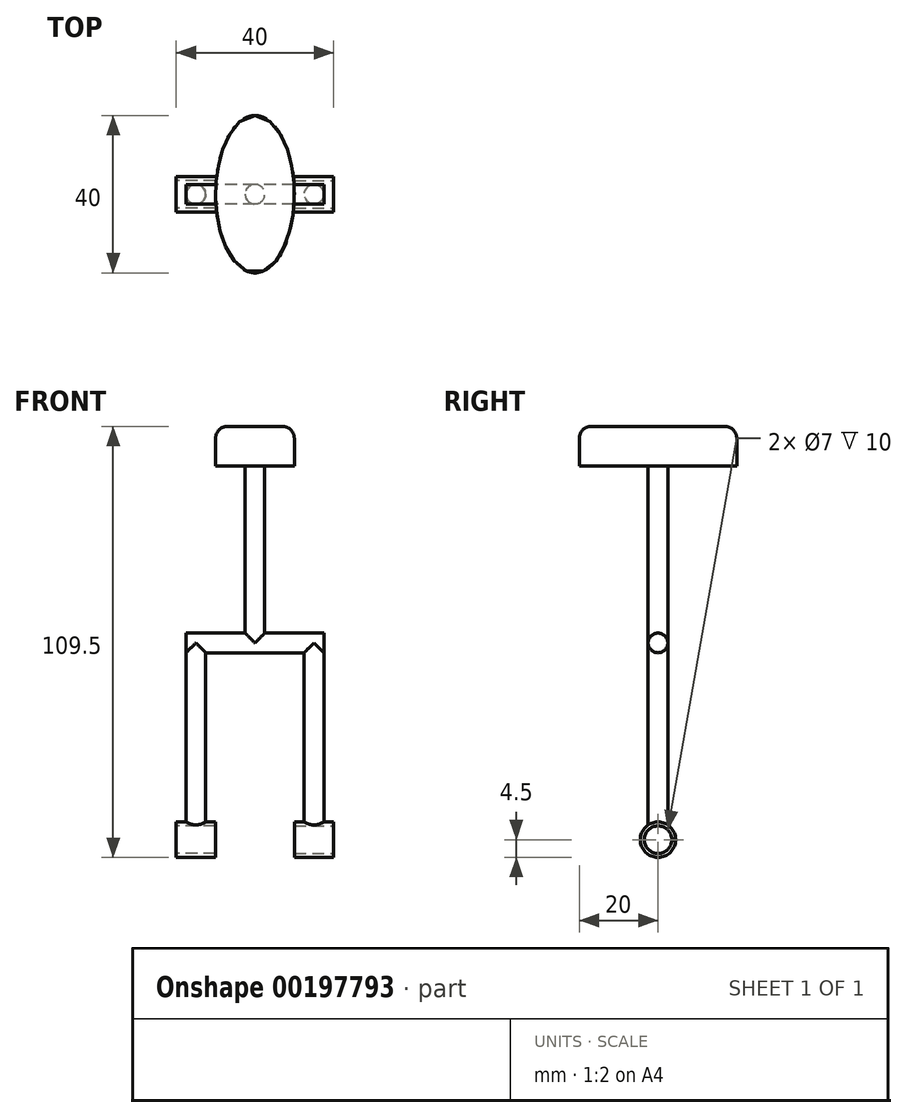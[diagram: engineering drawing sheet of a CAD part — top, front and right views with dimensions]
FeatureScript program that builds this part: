
annotation { "Feature Type Name" : "Feature", "Feature Type Description" : "" }
export const myFeature = defineFeature(function(context is Context, id is Id, definition is map)
    precondition{}
    {
        {
            var Q0;
            Q0=qCreatedBy(makeId("Top.planeOp"),FACE);
            var sketch = newSketch(context, id + "F0", { "sketchPlane" : qUnion([Q0])});
            skEllipse(sketch, "E0", {"center": v(0, 0) * mm, "majorRadius": 20 * mm, "minorRadius": 10 * mm, "majorAxis": v(0, 1)});
            skLineSegment(sketch, "E1", {"start": v(0, 0) * mm, "end": v(0, 20) * mm, "construction": true});
            skSolve(sketch);
        }
        {
            var Q0;
            Q0 = qSketchRegion(id + "F0", true);
            extrude(context, id + "F1", {"entities" : qUnion([Q0]), "depth" : 10 * mm});
        }
        {
            var Q0;
            Q0=makeQuery(id+"F1.opExtrude","CAP_FACE",FACE,{"disambiguationData":[OSD([sQuery(id+"F0.wireOp",EDGE,"E0")])],"isStart":true});
            var sketch = newSketch(context, id + "F2", { "sketchPlane" : qUnion([Q0])});
            skCircle(sketch, "E2", {"center": v(0, 0) * mm, "radius": 2.5 * mm});
            skSolve(sketch);
        }
        {
            var Q0;
            Q0 = qSketchRegion(id + "F2", true);
            extrude(context, id + "F3", {"entities" : qUnion([Q0]), "operationType" : NewBodyOperationType.ADD, "depth" : 45 * mm});
        }
        {
            var Q0;
            Q0=qCreatedBy(makeId("Right.planeOp"),FACE);
            var sketch = newSketch(context, id + "F4", { "sketchPlane" : qUnion([Q0])});
            skCircle(sketch, "E3", {"center": v(0, -45) * mm, "radius": 2.5 * mm});
            skSolve(sketch);
        }
        {
            var Q0;
            Q0 = qSketchRegion(id + "F4", true);
            extrude(context, id + "F5", {"entities" : qUnion([Q0]), "operationType" : NewBodyOperationType.ADD, "depth" : 17.5 * mm, "hasSecondDirection" : true, "secondDirectionOppositeDirection" : true, "secondDirectionDepth" : 17.5 * mm});
        }
        {
            var Q0;
            Q0=qCreatedBy(makeId("Top.planeOp"),FACE);
            cPlane(context, id + "F6", {"entities" : qUnion([Q0]), "cplaneType" : CPlaneType.OFFSET, "offset" : 45 * mm, "oppositeDirection" : true, "width" : 150 * mm, "height" : 150 * mm});
        }
        {
            var Q0;
            Q0=qCreatedBy(id+"F6.planeOp",FACE);
            var sketch = newSketch(context, id + "F7", { "sketchPlane" : qUnion([Q0])});
            skCircle(sketch, "E4", {"center": v(15, 0) * mm, "radius": 2.5 * mm});
            skCircle(sketch, "E5", {"center": v(-15, 0) * mm, "radius": 2.5 * mm});
            skSolve(sketch);
        }
        {
            var Q0;
            Q0 = qSketchRegion(id + "F7", true);
            extrude(context, id + "F8", {"entities" : qUnion([Q0]), "operationType" : NewBodyOperationType.ADD, "oppositeDirection" : true, "depth" : 50 * mm});
        }
        {
            var Q0;
            Q0=makeQuery(id+"F1.opExtrude","SWEPT_BODY",BODY,{"disambiguationData":[OSD([sQuery(id+"F0.wireOp",EDGE,"E0")])]});
            transform(context, id + "F9", {"entities" : qUnion([Q0]), "transformType" : TransformType.TRANSLATION_3D, "dx" : 0 * mm, "dy" : 0 * mm, "dz" : 45 * mm, "makeCopy" : false});
        }
        {
            var Q0;
            Q0=qCreatedBy(makeId("Right.planeOp"),FACE);
            cPlane(context, id + "F10", {"entities" : qUnion([Q0]), "cplaneType" : CPlaneType.OFFSET, "offset" : 15 * mm, "width" : 150 * mm, "height" : 150 * mm});
        }
        {
            var Q0;
            Q0=qCreatedBy(makeId("Right.planeOp"),FACE);
            cPlane(context, id + "F11", {"entities" : qUnion([Q0]), "cplaneType" : CPlaneType.OFFSET, "offset" : 15 * mm, "oppositeDirection" : true, "width" : 150 * mm, "height" : 150 * mm});
        }
        {
            var Q0;
            Q0=qCreatedBy(id+"F10.planeOp",FACE);
            var sketch = newSketch(context, id + "F12", { "sketchPlane" : qUnion([Q0])});
            skCircle(sketch, "E6", {"center": v(0, -50) * mm, "radius": 4.5 * mm});
            skSolve(sketch);
        }
        {
            var Q0;
            Q0 = qSketchRegion(id + "F12", true);
            extrude(context, id + "F13", {"entities" : qUnion([Q0]), "operationType" : NewBodyOperationType.ADD, "depth" : 5 * mm, "hasSecondDirection" : true, "secondDirectionOppositeDirection" : true, "secondDirectionDepth" : 5 * mm});
        }
        {
            var Q0;
            Q0=makeQuery(id+"F13.opExtrude","CAP_FACE",FACE,{"disambiguationData":[OSD([sQuery(id+"F12.wireOp",EDGE,"E6")])],"isStart":false});
            var sketch = newSketch(context, id + "F14", { "sketchPlane" : qUnion([Q0])});
            skCircle(sketch, "E7", {"center": v(0, -50) * mm, "radius": 3.5 * mm});
            skSolve(sketch);
        }
        {
            var Q0;
            Q0 = qSketchRegion(id + "F14", true);
            extrude(context, id + "F15", {"entities" : qUnion([Q0]), "operationType" : NewBodyOperationType.REMOVE, "oppositeDirection" : true, "depth" : 25 * mm});
        }
        {
            var Q0;
            Q0=qCreatedBy(id+"F11.planeOp",FACE);
            var sketch = newSketch(context, id + "F16", { "sketchPlane" : qUnion([Q0])});
            skCircle(sketch, "E8", {"center": v(0, -50) * mm, "radius": 4.5 * mm});
            skSolve(sketch);
        }
        {
            var Q0;
            Q0 = qSketchRegion(id + "F16", true);
            extrude(context, id + "F17", {"entities" : qUnion([Q0]), "operationType" : NewBodyOperationType.ADD, "depth" : 5 * mm, "hasSecondDirection" : true, "secondDirectionOppositeDirection" : true, "secondDirectionDepth" : 5 * mm});
        }
        {
            var Q0;
            Q0=makeQuery(id+"F17.opExtrude","CAP_FACE",FACE,{"disambiguationData":[OSD([sQuery(id+"F16.wireOp",EDGE,"E8")])],"isStart":true});
            var sketch = newSketch(context, id + "F18", { "sketchPlane" : qUnion([Q0])});
            skCircle(sketch, "E9", {"center": v(0, -50) * mm, "radius": 3.5 * mm});
            skSolve(sketch);
        }
        {
            var Q0;
            Q0 = qSketchRegion(id + "F18", true);
            extrude(context, id + "F19", {"entities" : qUnion([Q0]), "operationType" : NewBodyOperationType.REMOVE, "oppositeDirection" : true, "depth" : 25 * mm});
        }
        {
            var Q0;
            Q0=makeQuery(id+"F1.opExtrude","CAP_EDGE",EDGE,{"disambiguationData":[OSD([sQuery(id+"F0.wireOp",EDGE,"E0")])],"isStart":false});
            fillet(context, id + "F20", {"entities" : qUnion([Q0]), "radius" : 3 * mm, "tangentPropagation" : true, "allowEdgeOverflow" : false});
        }
    });
